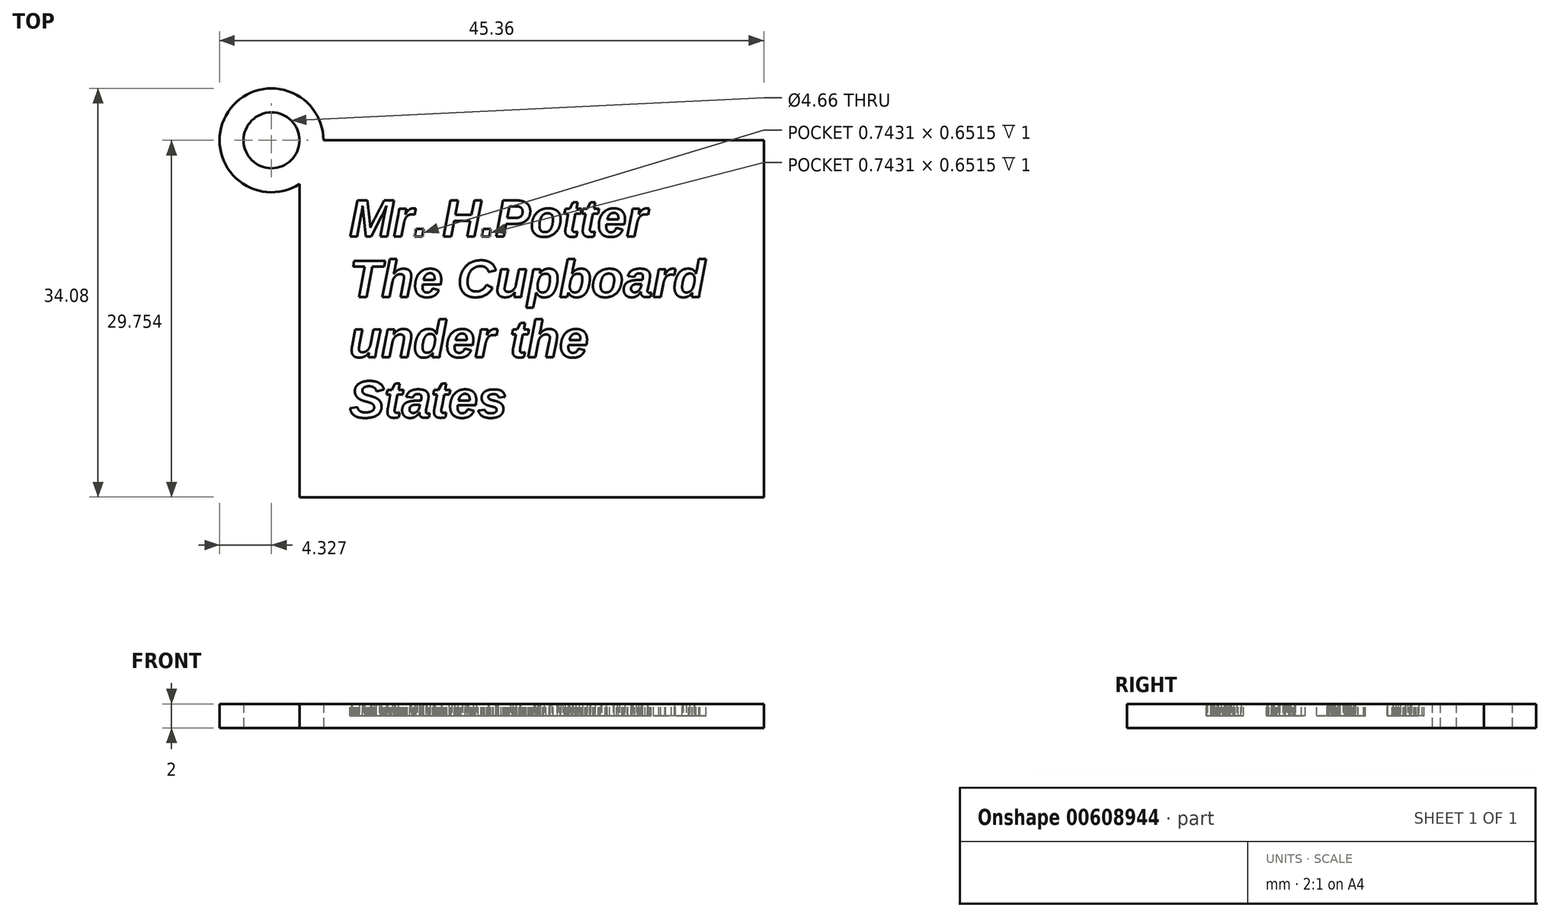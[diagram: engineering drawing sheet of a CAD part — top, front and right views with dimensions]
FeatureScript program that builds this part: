
annotation { "Feature Type Name" : "Feature", "Feature Type Description" : "" }
export const myFeature = defineFeature(function(context is Context, id is Id, definition is map)
    precondition{}
    {
        {
            var Q0;
            Q0=qCreatedBy(makeId("Top.planeOp"),FACE);
            var sketch = newSketch(context, id + "F0", { "sketchPlane" : qUnion([Q0])});
            skLineSegment(sketch, "E0.bottom", {"start": v(-23.7, 25.44) * mm, "end": v(15, 25.44) * mm});
            skLineSegment(sketch, "E0.top", {"start": v(-23.7, -4.31) * mm, "end": v(15, -4.31) * mm});
            skLineSegment(sketch, "E0.left", {"start": v(-23.7, 25.44) * mm, "end": v(-23.7, -4.31) * mm});
            skLineSegment(sketch, "E0.right", {"start": v(15, 25.44) * mm, "end": v(15, -4.31) * mm});
            skCircle(sketch, "E1", {"center": v(-26.03, 25.44) * mm, "radius": 2.33 * mm});
            skCircle(sketch, "E2", {"center": v(-26.03, 25.44) * mm, "radius": 4.33 * mm});
            skSolve(sketch);
        }
        {
            var Q0;
            {var subQ1=sQuery(id+"F0.wireOp",EDGE,"E0.bottom");var subQ3=sQuery(id+"F0.wireOp",EDGE,"E2");var subQ4=makeQuery(id+"F0.imprint","INTERSECT",VERTEX,{"derivedFrom":[subQ1,subQ3]});Q0=makeQuery(id+"F0.imprint","IMPRINT",FACE,{"disambiguationData":[TD([[makeQuery(id+"F0.imprint","IMPRINT",EDGE,{"disambiguationData":[TD([[subQ4,1.0]])],"derivedFrom":subQ3}),1.0]])]});}
            var Q1;
            {var subQ0=sQuery(id+"F0.wireOp",EDGE,"E1");Q1=makeQuery(id+"F0.imprint","IMPRINT",FACE,{"disambiguationData":[TD([[makeQuery(id+"F0.imprint","IMPRINT",EDGE,{"derivedFrom":subQ0}),-1.0]])]});}
            var Q2;
            {var subQ2=sQuery(id+"F0.wireOp",EDGE,"E0.top");Q2=makeQuery(id+"F0.imprint","IMPRINT",FACE,{"disambiguationData":[TD([[makeQuery(id+"F0.imprint","IMPRINT",EDGE,{"derivedFrom":subQ2}),1.0]])]});}
            extrude(context, id + "F1", {"entities" : qUnion([Q0, Q1, Q2]), "depth" : 2 * mm, "offsetDistance" : 25 * mm});
        }
        {
            var Q0;
            Q0=makeQuery(id+"F1.opExtrude","CAP_FACE",FACE,{"disambiguationData":[OSD([sQuery(id+"F0.wireOp",EDGE,"E0.bottom"),sQuery(id+"F0.wireOp",EDGE,"E0.top"),sQuery(id+"F0.wireOp",EDGE,"E0.left"),sQuery(id+"F0.wireOp",EDGE,"E0.right"),sQuery(id+"F0.wireOp",EDGE,"E1"),sQuery(id+"F0.wireOp",EDGE,"E2")])],"isStart":false});
            var sketch = newSketch(context, id + "F2", { "sketchPlane" : qUnion([Q0])});
            skText(sketch, "E3", { "text": "Mr. H.Potter\nThe Cupboard\nunder the\nStates", "fontName": "Arimo-BoldItalic.ttf"});
            const initialGuessF2  = {"E3": [-0.01954, 0.01742, 1, 0, 0.00315]};
            skSetInitialGuess(sketch, initialGuessF2);
            skSolve(sketch);
        }
        {
            var Q0;
            Q0 = qSketchRegion(id + "F2", true);
            extrude(context, id + "F3", {"entities" : qUnion([Q0]), "operationType" : NewBodyOperationType.REMOVE, "oppositeDirection" : true, "depth" : 1 * mm, "offsetDistance" : 25 * mm});
        }
    });
